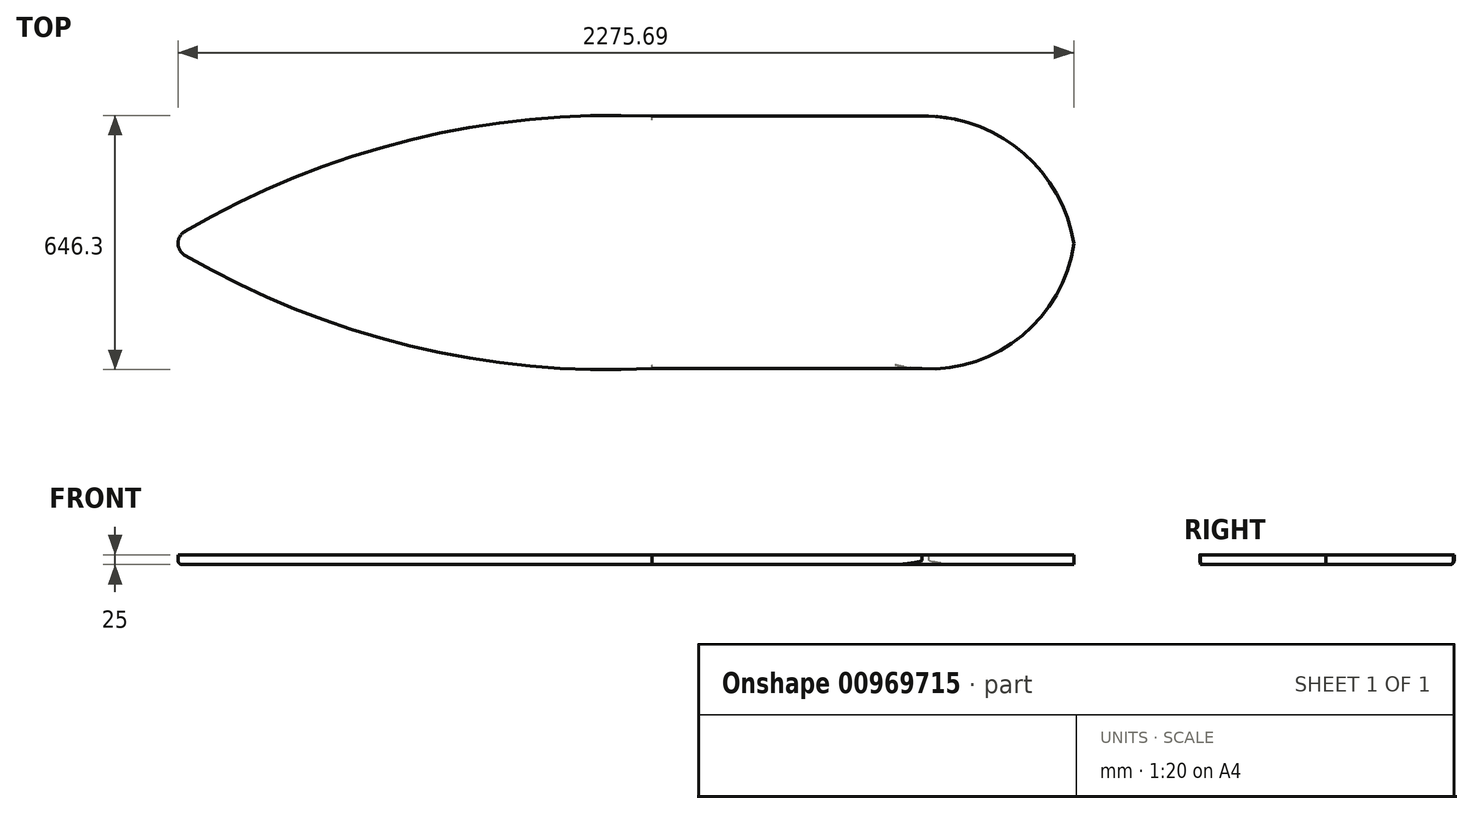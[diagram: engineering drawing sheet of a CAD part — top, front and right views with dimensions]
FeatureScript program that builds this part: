
annotation { "Feature Type Name" : "Feature", "Feature Type Description" : "" }
export const myFeature = defineFeature(function(context is Context, id is Id, definition is map)
    precondition{}
    {
        {
            var Q0;
            Q0=qCreatedBy(makeId("Top.planeOp"),FACE);
            var sketch = newSketch(context, id + "F0", { "sketchPlane" : qUnion([Q0])});
            skLineSegment(sketch, "E0.bottom", {"start": v(-196.93, 323.31) * mm, "end": v(703.07, 323.31) * mm});
            skLineSegment(sketch, "E0.top", {"start": v(-213.1, -318.07) * mm, "end": v(686.9, -318.07) * mm});
            skArc(sketch, "E1", {"start": v(0, 323.31) * mm, "mid": v(-614.15, 262.8) * mm, "end": v(-1185.81, 30.34) * mm});
            skArc(sketch, "E2", {"start": v(-1185.68, -30.12) * mm, "mid": v(-613.42, -260.06) * mm, "end": v(0.58, -318.07) * mm});
            skPoint(sketch, "E3.orphan", {"position": v(-685.74, -318.07) * mm});
            skArc(sketch, "E4", {"start": v(1072.58, 0) * mm, "mid": v(946.23, 228.4) * mm, "end": v(703.07, 323.31) * mm});
            skArc(sketch, "E5", {"start": v(686.9, -318.07) * mm, "mid": v(941.59, -234.03) * mm, "end": v(1072.58, 0) * mm});
            skPoint(sketch, "E6.visualSharp", {"position": v(-1235.98, 0) * mm});
            skArc(sketch, "E6.filletArc", {"start": v(-1185.81, 30.34) * mm, "mid": v(-1203.1, 0.07) * mm, "end": v(-1185.68, -30.12) * mm});
            skPoint(sketch, "E7.end.orphan", {"position": v(1072.58, -318.07) * mm});
            skPoint(sketch, "E8.end.orphan", {"position": v(1072.58, 323.31) * mm});
            skSolve(sketch);
        }
        {
            var Q0;
            Q0 = qSketchRegion(id + "F0", true);
            extrude(context, id + "F1", {"entities" : qUnion([Q0]), "depth" : 25 * mm, "offsetDistance" : 25 * mm});
        }
        {
            var Q0;
            Q0=makeQuery(id+"F1.opExtrude","CAP_EDGE",EDGE,{"disambiguationData":[OSD([sQuery(id+"F0.wireOp",EDGE,"E6.filletArc")])],"isStart":true});
            fillet(context, id + "F2", {"entities" : qUnion([Q0]), "radius" : 10 * mm, "tangentPropagation" : true, "allowEdgeOverflow" : false});
        }
    });
